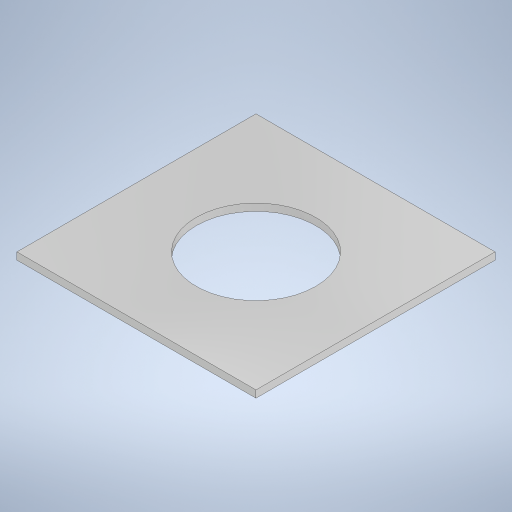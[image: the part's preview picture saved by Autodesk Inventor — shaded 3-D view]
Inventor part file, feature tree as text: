
AUTODESK INVENTOR PART (.ipt)
format: ipt  version: 2024 (Build 280153000, 153)  size: 223,232 bytes
history: native  units: in
note: dims shown in document units (in); Inventor stores cm internally (conversion verified against a paired STEP export)
features: sketch x2, extrude x1, hole x1
ambient origin geometry x8: Origin, YZ Plane, XZ Plane, XY Plane, X Axis, Y Axis, Z Axis, Center Point
bodies: Solid1 (feature_tree)
feature tree (4):
  extrude  "Extrusion1"  Depth=3.937in
  hole  "Hole1"  [1 undecoded]
  sketch  "Sketch1"  dims[d0=3.937in d1=3.937in]
  sketch  "Sketch2"  dims[d2=0.1181in d3=0.0in d4=1.9685in d5=0.2953in d6=0.1476in d7=0.0984in d8=90.0deg d9=0.3937in d10=0.8108in]
note: 1 required parameter value undecoded (feature->parameter linkage not recoverable at this tier; creation-order binding heuristic only, values carry confidence <= 0.55)
